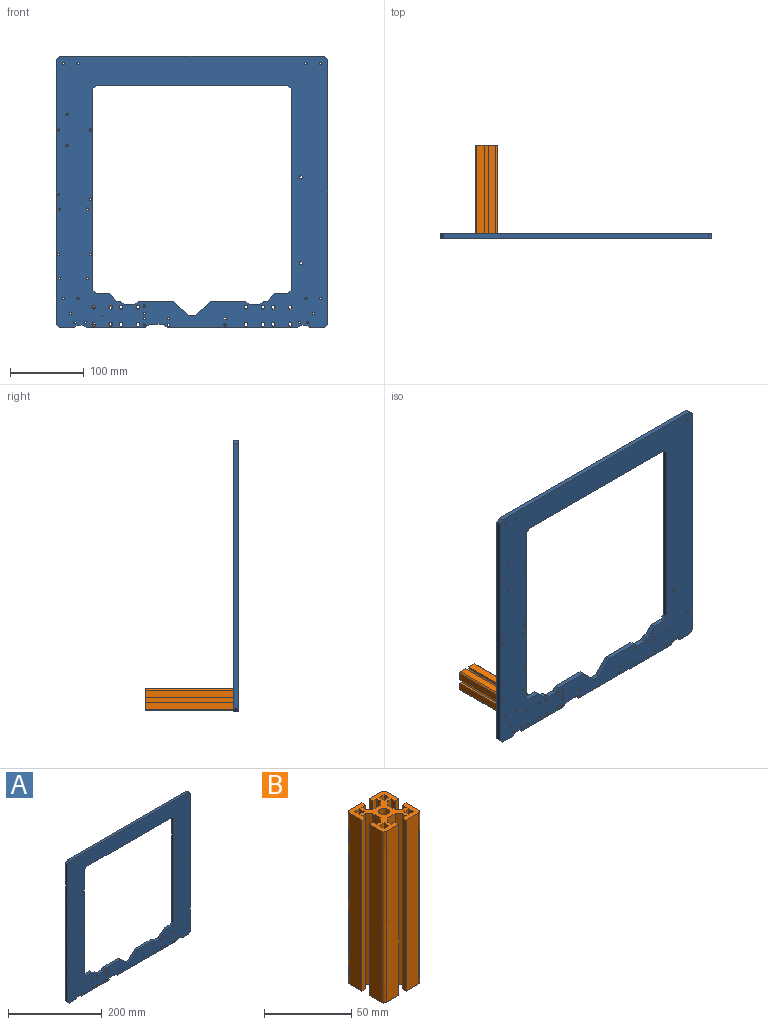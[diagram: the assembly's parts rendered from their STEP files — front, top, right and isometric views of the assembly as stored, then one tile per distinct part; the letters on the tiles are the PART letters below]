
ASSEMBLY  parts=2 mates=1
PART A: 99 faces, bbox 370x6.5x370 mm
  f0: plane 6.5x5mm, normal (-0.71,0,0.71), area 46mm2, adj f1,f96,f97,f98
  f1: plane 360x6.5mm, normal (-1,0,0), area 2340mm2, adj f0,f2,f97,f98
  f2: plane 6.5x5mm, normal (-0.71,0,-0.71), area 46mm2, adj f1,f3,f97,f98
  f3: plane 20x6.5mm, normal (0,0,-1), area 130mm2, adj f2,f4,f97,f98
  f4: plane 6.5x4mm, normal (0.71,0,-0.71), area 36.8mm2, adj f3,f5,f97,f98
  f5: plane 8x6.5mm, normal (0,0,-1), area 52mm2, adj f4,f6,f97,f98
  f6: plane 6.5x4mm, normal (-0.71,0,-0.71), area 36.8mm2, adj f5,f7,f97,f98
  f7: plane 81x6.5mm, normal (0,0,-1), area 526.5mm2, adj f6,f8,f97,f98
  f8: plane 6.5x5mm, normal (0.71,0,-0.71), area 46mm2, adj f7,f9,f97,f98
  f9: plane 19x6.5mm, normal (0,0,-1), area 123.5mm2, adj f8,f10,f97,f98
  f10: plane 6.5x5mm, normal (-0.71,0,-0.71), area 46mm2, adj f9,f11,f97,f98
  f11: plane 178x6.5mm, normal (0,0,-1), area 1157mm2, adj f10,f12,f97,f98
  f12: plane 6.5x4mm, normal (0.71,0,-0.71), area 36.8mm2, adj f11,f13,f97,f98
  f13: plane 8x6.5mm, normal (0,0,-1), area 52mm2, adj f12,f14,f97,f98
  f14: plane 6.5x4mm, normal (-0.71,0,-0.71), area 36.8mm2, adj f13,f15,f97,f98
  f15: plane 20x6.5mm, normal (0,0,-1), area 130mm2, adj f14,f16,f97,f98
  f16: plane 6.5x5mm, normal (0.71,0,-0.71), area 46mm2, adj f15,f17,f97,f98
  f17: plane 360x6.5mm, normal (1,0,0), area 2340mm2, adj f16,f18,f97,f98
  f18: plane 6.5x5mm, normal (0.71,0,0.71), area 46mm2, adj f17,f96,f97,f98
  f19: plane 6.5x5mm, normal (-0.71,0,0.71), area 46mm2, adj f20,f42,f97,f98
  f20: plane 14x6.5mm, normal (0,0,1), area 91mm2, adj f19,f21,f97,f98
  f21: plane 6.5x5mm, normal (0.71,0,0.71), area 46mm2, adj f20,f22,f97,f98
  f22: plane 6.5x5mm, normal (0,0,1), area 32.5mm2, adj f21,f23,f97,f98
  f23: plane 10x10mm, normal (0.71,0,0.71), area 91.9mm2, adj f22,f24,f97,f98
  f24: plane 18x6.5mm, normal (0,0,1), area 117mm2, adj f23,f25,f97,f98
  f25: plane 6.5x5mm, normal (0.71,0,0.71), area 46mm2, adj f24,f26,f97,f98
  f26: plane 273.5x6.5mm, normal (1,0,0), area 1777.7mm2, adj f25,f27,f97,f98
  f27: plane 6.5x5mm, normal (0.71,0,-0.71), area 46mm2, adj f26,f28,f97,f98
  f28: plane 260x6.5mm, normal (0,0,-1), area 1690mm2, adj f27,f29,f97,f98
  f29: plane 6.5x5mm, normal (-0.71,0,-0.71), area 46mm2, adj f28,f30,f97,f98
  f30: plane 273.5x6.5mm, normal (-1,0,0), area 1777.7mm2, adj f29,f31,f97,f98
  f31: plane 6.5x5mm, normal (-0.71,0,0.71), area 46mm2, adj f30,f32,f97,f98
  f32: plane 18x6.5mm, normal (0,0,1), area 117mm2, adj f31,f33,f97,f98
  f33: plane 10x10mm, normal (-0.71,0,0.71), area 91.9mm2, adj f32,f34,f97,f98
  f34: plane 6.5x5mm, normal (0,0,1), area 32.5mm2, adj f33,f35,f97,f98
  f35: plane 6.5x5mm, normal (-0.71,0,0.71), area 46mm2, adj f34,f36,f97,f98
  f36: plane 14x6.5mm, normal (0,0,1), area 91mm2, adj f35,f37,f97,f98
  f37: plane 6.5x5mm, normal (0.71,0,0.71), area 46mm2, adj f36,f38,f97,f98
  f38: plane 48x6.5mm, normal (0,0,1), area 312mm2, adj f37,f39,f97,f98
  f39: plane 20x20mm, normal (-0.71,0,0.71), area 183.8mm2, adj f38,f40,f97,f98
  f40: plane 10x6.5mm, normal (0,0,1), area 65mm2, adj f39,f41,f97,f98
  f41: plane 20x20mm, normal (0.71,0,0.71), area 183.8mm2, adj f40,f42,f97,f98
  f42: plane 48x6.5mm, normal (0,0,1), area 312mm2, adj f19,f41,f97,f98
  f43: cylinder r=2.55mm len=6.5mm, axis (0,1,0), area 104.1mm2, adj f97,f98
  f44: cylinder r=2.55mm len=6.5mm, axis (0,1,0), area 104.1mm2, adj f97,f98
  f45: cylinder r=2.55mm len=6.5mm, axis (0,1,0), area 104.1mm2, adj f97,f98
  f46: cylinder r=2.55mm len=6.5mm, axis (0,1,0), area 104.1mm2, adj f97,f98
  f47: cylinder r=2.55mm len=6.5mm, axis (0,1,0), area 104.1mm2, adj f97,f98
  f48: cylinder r=2.55mm len=6.5mm, axis (0,1,0), area 104.1mm2, adj f97,f98
  f49: cylinder r=2.55mm len=6.5mm, axis (0,1,0), area 104.1mm2, adj f97,f98
  f50: cylinder r=2.55mm len=6.5mm, axis (0,1,0), area 104.1mm2, adj f97,f98
  f51: cylinder r=1.5mm len=6.5mm, axis (0,1,0), area 61.3mm2, adj f97,f98
  f52: cylinder r=1.5mm len=6.5mm, axis (0,1,0), area 61.3mm2, adj f97,f98
  f53: cylinder r=1.5mm len=6.5mm, axis (0,1,0), area 61.3mm2, adj f97,f98
  f54: cylinder r=1.5mm len=6.5mm, axis (0,1,0), area 61.3mm2, adj f97,f98
  f55: cylinder r=1.5mm len=6.5mm, axis (0,1,0), area 61.3mm2, adj f97,f98
  f56: cylinder r=1.5mm len=6.5mm, axis (0,1,0), area 61.3mm2, adj f97,f98
  f57: cylinder r=1.5mm len=6.5mm, axis (0,1,0), area 61.3mm2, adj f97,f98
  f58: cylinder r=1.5mm len=6.5mm, axis (0,1,0), area 61.3mm2, adj f97,f98
  f59: cylinder r=1.5mm len=6.5mm, axis (0,1,0), area 61.3mm2, adj f97,f98
  f60: cylinder r=1.5mm len=6.5mm, axis (0,1,0), area 61.3mm2, adj f97,f98
  f61: cylinder r=1.5mm len=6.5mm, axis (0,1,0), area 61.3mm2, adj f97,f98
  f62: cylinder r=1.6mm len=6.5mm, axis (0,1,0), area 65.3mm2, adj f97,f98
  f63: cylinder r=1.6mm len=6.5mm, axis (0,1,0), area 65.3mm2, adj f97,f98
  f64: cylinder r=1.6mm len=6.5mm, axis (0,1,0), area 65.3mm2, adj f97,f98
  f65: cylinder r=2.1mm len=6.5mm, axis (0,1,0), area 85.8mm2, adj f97,f98
  f66: cylinder r=1.6mm len=6.5mm, axis (0,1,0), area 65.3mm2, adj f97,f98
  f67: cylinder r=1.6mm len=6.5mm, axis (0,1,0), area 65.3mm2, adj f97,f98
  f68: cylinder r=1.6mm len=6.5mm, axis (0,1,0), area 65.3mm2, adj f97,f98
  f69: cylinder r=0.5mm len=6.5mm, axis (0,1,0), area 20.4mm2, adj f97,f98
  f70: cylinder r=1.6mm len=6.5mm, axis (0,1,0), area 65.3mm2, adj f97,f98
  f71: cylinder r=1.6mm len=6.5mm, axis (0,1,0), area 65.3mm2, adj f97,f98
  f72: cylinder r=2.1mm len=6.5mm, axis (0,1,0), area 85.8mm2, adj f97,f98
  f73: cylinder r=1.6mm len=6.5mm, axis (0,1,0), area 65.3mm2, adj f97,f98
  f74: cylinder r=1.6mm len=6.5mm, axis (0,1,0), area 65.3mm2, adj f97,f98
  f75: cylinder r=1.6mm len=6.5mm, axis (0,1,0), area 65.3mm2, adj f97,f98
  f76: cylinder r=1.6mm len=6.5mm, axis (0,1,0), area 65.3mm2, adj f97,f98
  f77: cylinder r=1.5mm len=6.5mm, axis (0,1,0), area 61.3mm2, adj f97,f98
  f78: cylinder r=1.5mm len=6.5mm, axis (0,1,0), area 61.3mm2, adj f97,f98
  f79: cylinder r=1.5mm len=6.5mm, axis (0,1,0), area 61.3mm2, adj f97,f98
  f80: cylinder r=1.5mm len=6.5mm, axis (0,1,0), area 61.3mm2, adj f97,f98
  f81: cylinder r=1.5mm len=6.5mm, axis (0,1,0), area 61.3mm2, adj f97,f98
  f82: cylinder r=1.5mm len=6.5mm, axis (0,1,0), area 61.3mm2, adj f97,f98
  f83: cylinder r=1.5mm len=6.5mm, axis (0,1,0), area 61.3mm2, adj f97,f98
  f84: cylinder r=1.5mm len=6.5mm, axis (0,1,0), area 61.3mm2, adj f97,f98
  f85: cylinder r=1.5mm len=6.5mm, axis (0,1,0), area 61.3mm2, adj f97,f98
  f86: cylinder r=1.5mm len=6.5mm, axis (0,1,0), area 61.3mm2, adj f97,f98
  f87: cylinder r=1.5mm len=6.5mm, axis (0,1,0), area 61.3mm2, adj f97,f98
  f88: cylinder r=2.55mm len=6.5mm, axis (0,1,0), area 104.1mm2, adj f97,f98
  f89: cylinder r=2.55mm len=6.5mm, axis (0,1,0), area 104.1mm2, adj f97,f98
  f90: cylinder r=2.55mm len=6.5mm, axis (0,1,0), area 104.1mm2, adj f97,f98
  f91: cylinder r=2.55mm len=6.5mm, axis (0,1,0), area 104.1mm2, adj f97,f98
  f92: cylinder r=2.55mm len=6.5mm, axis (0,1,0), area 104.1mm2, adj f97,f98
  f93: cylinder r=2.55mm len=6.5mm, axis (0,1,0), area 104.1mm2, adj f97,f98
  f94: cylinder r=2.55mm len=6.5mm, axis (0,1,0), area 104.1mm2, adj f97,f98
  f95: cylinder r=2.55mm len=6.5mm, axis (0,1,0), area 104.1mm2, adj f97,f98
  f96: plane 360x6.5mm, normal (0,0,1), area 2340mm2, adj f0,f18,f97,f98
  f97: plane 370x370mm, normal (0,-1,0), area 56601.6mm2, adj f0,f1,f2,f3,f4,f5,f6,f7
  f98: plane 370x370mm, normal (0,1,0), area 56601.6mm2, adj f0,f1,f2,f3,f4,f5,f6,f7
PART B: 67 faces, bbox 30x30x120 mm
  f0: plane 120x4mm, normal (-1,0,0), area 480mm2, adj f1,f64,f65,f66
  f1: plane 120x4mm, normal (0,-1,0), area 480mm2, adj f0,f2,f65,f66
  f2: plane 120x4mm, normal (1,0,0), area 480mm2, adj f1,f64,f65,f66
  f3: plane 120x4mm, normal (0,1,0), area 480mm2, adj f4,f59,f65,f66
  f4: plane 120x4mm, normal (-1,0,0), area 480mm2, adj f3,f5,f65,f66
  f5: plane 120x4mm, normal (0,-1,0), area 480mm2, adj f4,f59,f65,f66
  f6: extruded ~120x2mm, area 376.9mm2, adj f7,f61,f65,f66
  f7: plane 120x10mm, normal (0,1,0), area 1200mm2, adj f6,f8,f65,f66
  f8: plane 120x3mm, normal (1,0,0), area 360mm2, adj f7,f9,f65,f66
  f9: plane 120x3mm, normal (0,-1,0), area 360mm2, adj f8,f10,f65,f66
  f10: plane 120x3mm, normal (1,0,0), area 360mm2, adj f9,f11,f65,f66
  f11: plane 120x3mm, normal (0.71,0.71,0), area 509.1mm2, adj f10,f12,f65,f66
  f12: plane 120x6mm, normal (0,1,0), area 720mm2, adj f11,f13,f65,f66
  f13: plane 120x3mm, normal (-0.71,0.71,0), area 509.1mm2, adj f12,f14,f65,f66
  f14: plane 120x3mm, normal (-1,0,0), area 360mm2, adj f13,f15,f65,f66
  f15: plane 120x3mm, normal (0,-1,0), area 360mm2, adj f14,f16,f65,f66
  f16: plane 120x3mm, normal (-1,0,0), area 360mm2, adj f15,f17,f65,f66
  f17: plane 120x10mm, normal (0,1,0), area 1200mm2, adj f16,f18,f65,f66
  f18: extruded ~120x2mm, area 376.9mm2, adj f17,f19,f65,f66
  f19: plane 120x10mm, normal (1,0,0), area 1200mm2, adj f18,f20,f65,f66
  f20: plane 120x3mm, normal (0,-1,0), area 360mm2, adj f19,f21,f65,f66
  f21: plane 120x3mm, normal (-1,0,0), area 360mm2, adj f20,f22,f65,f66
  f22: plane 120x3mm, normal (0,-1,0), area 360mm2, adj f21,f23,f65,f66
  f23: plane 120x3mm, normal (0.71,-0.71,0), area 509.1mm2, adj f22,f24,f65,f66
  f24: plane 120x6mm, normal (1,0,0), area 720mm2, adj f23,f25,f65,f66
  f25: plane 120x3mm, normal (0.71,0.71,0), area 509.1mm2, adj f24,f26,f65,f66
  f26: plane 120x3mm, normal (0,1,0), area 360mm2, adj f25,f27,f65,f66
  f27: plane 120x3mm, normal (-1,0,0), area 360mm2, adj f26,f28,f65,f66
  f28: plane 120x3mm, normal (0,1,0), area 360mm2, adj f27,f29,f65,f66
  f29: plane 120x10mm, normal (1,0,0), area 1200mm2, adj f28,f30,f65,f66
  f30: extruded ~120x2mm, area 376.9mm2, adj f29,f31,f65,f66
  f31: plane 120x10mm, normal (0,-1,0), area 1200mm2, adj f30,f32,f65,f66
  f32: plane 120x3mm, normal (-1,0,0), area 360mm2, adj f31,f33,f65,f66
  f33: plane 120x3mm, normal (0,1,0), area 360mm2, adj f32,f34,f65,f66
  f34: plane 120x3mm, normal (-1,0,0), area 360mm2, adj f33,f35,f65,f66
  f35: plane 120x3mm, normal (-0.71,-0.71,0), area 509.1mm2, adj f34,f36,f65,f66
  f36: plane 120x6mm, normal (0,-1,0), area 720mm2, adj f35,f37,f65,f66
  f37: plane 120x3mm, normal (0.71,-0.71,0), area 509.1mm2, adj f36,f38,f65,f66
  f38: plane 120x3mm, normal (1,0,0), area 360mm2, adj f37,f39,f65,f66
  f39: plane 120x3mm, normal (0,1,0), area 360mm2, adj f38,f40,f65,f66
  f40: plane 120x3mm, normal (1,0,0), area 360mm2, adj f39,f41,f65,f66
  f41: plane 120x10mm, normal (0,-1,0), area 1200mm2, adj f40,f42,f65,f66
  f42: extruded ~120x2mm, area 376.9mm2, adj f41,f43,f65,f66
  f43: plane 120x10mm, normal (-1,0,0), area 1200mm2, adj f42,f44,f65,f66
  f44: plane 120x3mm, normal (0,1,0), area 360mm2, adj f43,f45,f65,f66
  f45: plane 120x3mm, normal (1,0,0), area 360mm2, adj f44,f46,f65,f66
  f46: plane 120x3mm, normal (0,1,0), area 360mm2, adj f45,f47,f65,f66
  f47: plane 120x3mm, normal (-0.71,0.71,0), area 509.1mm2, adj f46,f48,f65,f66
  f48: plane 120x6mm, normal (-1,0,0), area 720mm2, adj f47,f49,f65,f66
  f49: plane 120x3mm, normal (-0.71,-0.71,0), area 509.1mm2, adj f48,f50,f65,f66
  f50: plane 120x3mm, normal (0,-1,0), area 360mm2, adj f49,f51,f65,f66
  f51: plane 120x3mm, normal (1,0,0), area 360mm2, adj f50,f52,f65,f66
  f52: plane 120x3mm, normal (0,-1,0), area 360mm2, adj f51,f61,f65,f66
  f53: plane 120x4mm, normal (-1,0,0), area 480mm2, adj f54,f62,f65,f66
  f54: plane 120x4mm, normal (0,-1,0), area 480mm2, adj f53,f55,f65,f66
  f55: plane 120x4mm, normal (1,0,0), area 480mm2, adj f54,f62,f65,f66
  f56: plane 120x4mm, normal (0,-1,0), area 480mm2, adj f57,f63,f65,f66
  f57: plane 120x4mm, normal (1,0,0), area 480mm2, adj f56,f58,f65,f66
  f58: plane 120x4mm, normal (0,1,0), area 480mm2, adj f57,f63,f65,f66
  f59: plane 120x4mm, normal (1,0,0), area 480mm2, adj f3,f5,f65,f66
  f60: cylinder r=3mm len=120mm, axis (0,0,1), area 2261.9mm2, adj f65,f66
  f61: plane 120x10mm, normal (-1,0,0), area 1200mm2, adj f6,f52,f65,f66
  f62: plane 120x4mm, normal (0,1,0), area 480mm2, adj f53,f55,f65,f66
  f63: plane 120x4mm, normal (-1,0,0), area 480mm2, adj f56,f58,f65,f66
  f64: plane 120x4mm, normal (0,1,0), area 480mm2, adj f0,f2,f65,f66
  f65: plane 30x30mm, normal (0,0,-1), area 480.3mm2, adj f0,f1,f2,f3,f4,f5,f6,f7
  f66: plane 30x30mm, normal (0,0,1), area 480.3mm2, adj f0,f1,f2,f3,f4,f5,f6,f7
PLACE A t=(-24.79,-52.49,-7.26)mm
PLACE B rot(axis=(-1,0,0),90deg) t=(-152.88,-12.49,-164.88)mm
MATE planar B.f60 <-> A.f69  axis (0,-1,0) through (-152.88,-52.49,-164.88)mm
